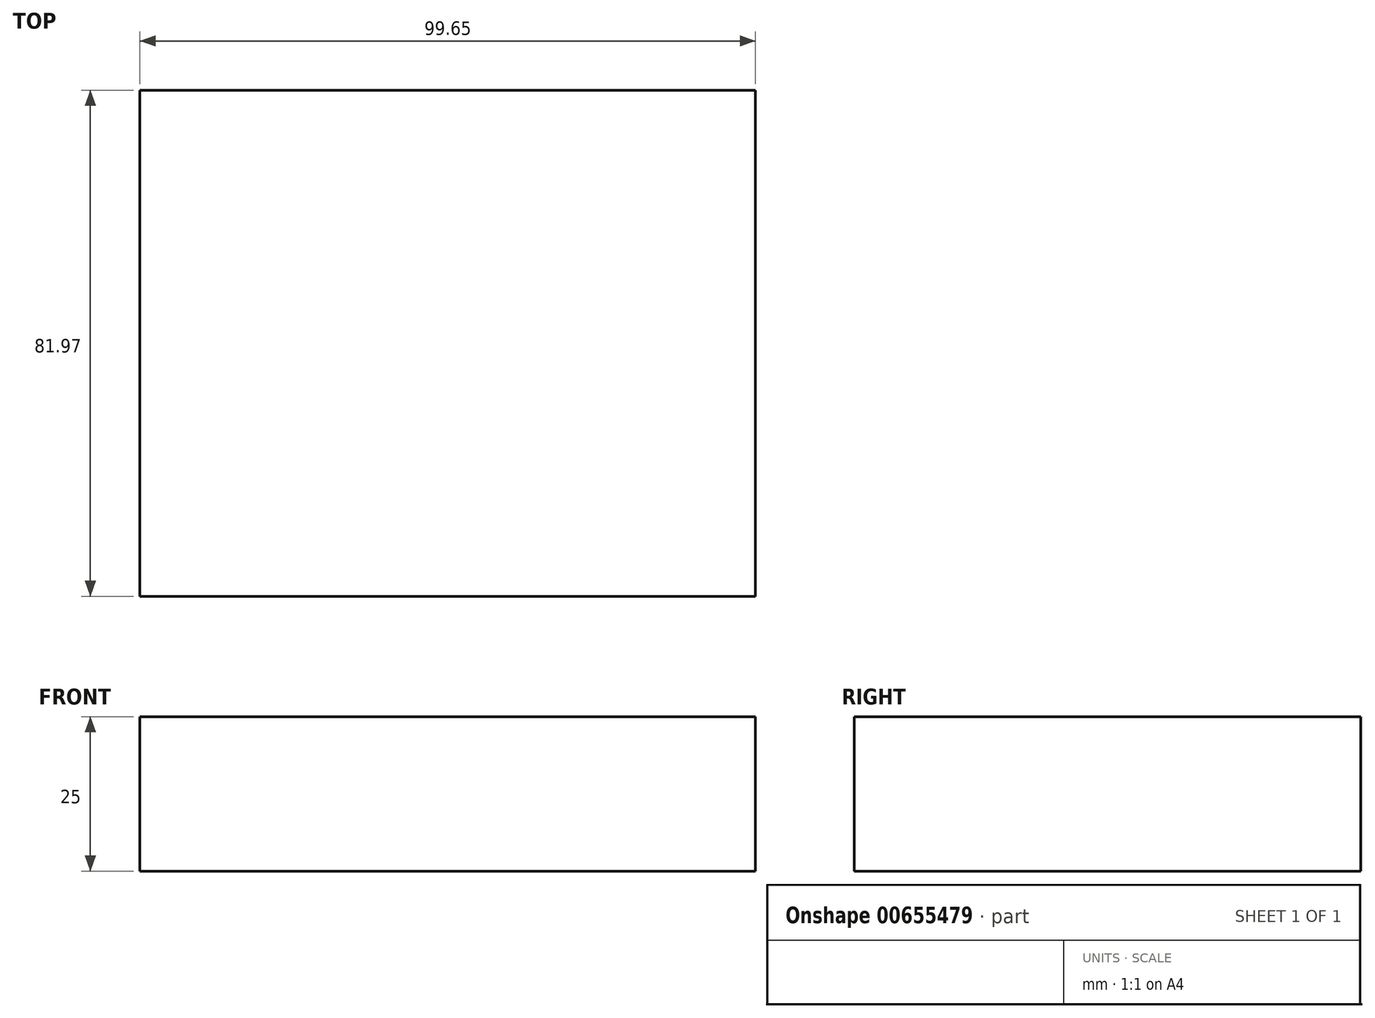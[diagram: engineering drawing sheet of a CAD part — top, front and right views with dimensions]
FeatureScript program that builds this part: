
annotation { "Feature Type Name" : "Feature", "Feature Type Description" : "" }
export const myFeature = defineFeature(function(context is Context, id is Id, definition is map)
    precondition{}
    {
        {
            var Q0;
            Q0=qCreatedBy(makeId("Top.planeOp"),FACE);
            var sketch = newSketch(context, id + "F0", { "sketchPlane" : qUnion([Q0])});
            skLineSegment(sketch, "E0.bottom", {"start": v(-18.74, 37.33) * mm, "end": v(80.9, 37.33) * mm});
            skLineSegment(sketch, "E0.top", {"start": v(-18.74, -44.64) * mm, "end": v(80.9, -44.64) * mm});
            skLineSegment(sketch, "E0.left", {"start": v(-18.74, 37.33) * mm, "end": v(-18.74, -44.64) * mm});
            skLineSegment(sketch, "E0.right", {"start": v(80.9, 37.33) * mm, "end": v(80.9, -44.64) * mm});
            skSolve(sketch);
        }
        {
            var Q0;
            Q0 = qSketchRegion(id + "F0", true);
            extrude(context, id + "F1", {"entities" : qUnion([Q0]), "oppositeDirection" : true, "depth" : 25 * mm, "offsetDistance" : 25 * mm});
        }
    });
